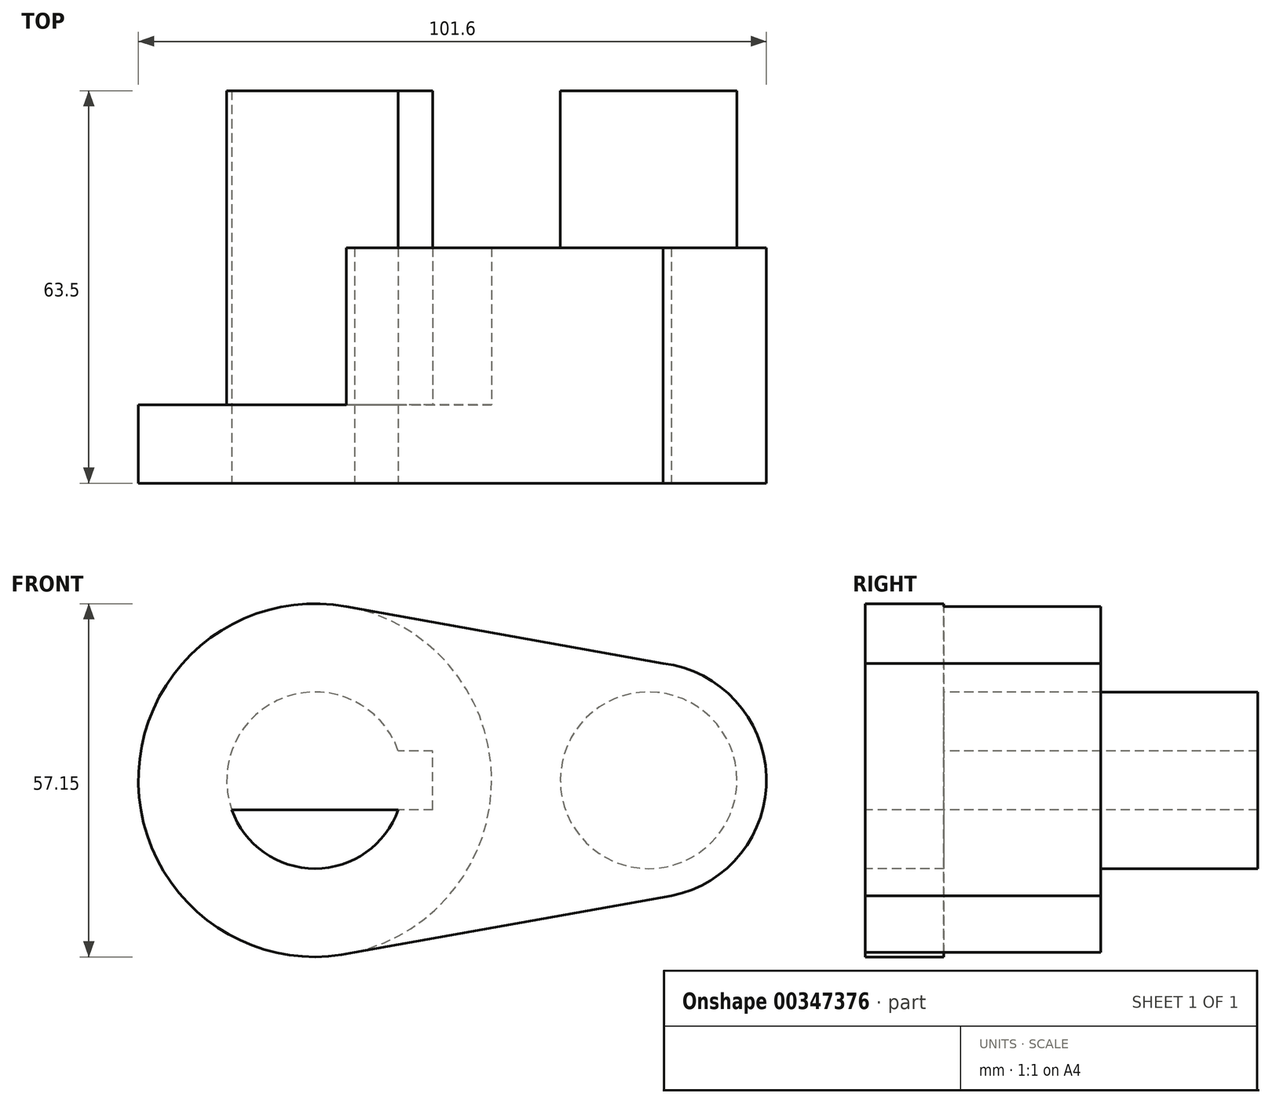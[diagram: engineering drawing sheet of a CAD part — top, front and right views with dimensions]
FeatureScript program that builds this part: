
annotation { "Feature Type Name" : "Feature", "Feature Type Description" : "" }
export const myFeature = defineFeature(function(context is Context, id is Id, definition is map)
    precondition{}
    {
        {
            var Q0;
            Q0=qCreatedBy(makeId("Front.planeOp"),FACE);
            var sketch = newSketch(context, id + "F0", { "sketchPlane" : qUnion([Q0])});
            skCircle(sketch, "E0", {"center": v(-15.51, -0.02) * mm, "radius": 28.58 * mm});
            skCircle(sketch, "E1", {"center": v(38.46, -0.02) * mm, "radius": 19.05 * mm});
            skCircle(sketch, "E2", {"center": v(-15.51, -0.02) * mm, "radius": 14.29 * mm});
            skCircle(sketch, "E3", {"center": v(38.46, -0.02) * mm, "radius": 14.29 * mm});
            skLineSegment(sketch, "E4.bottom", {"start": v(3.54, -4.79) * mm, "end": v(-34.56, -4.79) * mm});
            skLineSegment(sketch, "E4.top", {"start": v(3.54, 4.74) * mm, "end": v(-34.56, 4.74) * mm});
            skLineSegment(sketch, "E4.left", {"start": v(3.54, -4.79) * mm, "end": v(3.54, 4.74) * mm});
            skLineSegment(sketch, "E4.right", {"start": v(-34.56, -4.79) * mm, "end": v(-34.56, 4.74) * mm});
            skLineSegment(sketch, "E5", {"start": v(-10.46, 28.1) * mm, "end": v(40.77, 18.89) * mm});
            skLineSegment(sketch, "E6", {"start": v(-9.1, -27.87) * mm, "end": v(42.14, -18.71) * mm});
            skSolve(sketch);
        }
        {
            var Q0;
            {var subQ0=sQuery(id+"F0.wireOp",EDGE,"E4.top");var subQ1=sQuery(id+"F0.wireOp",EDGE,"E2");var subQ2=makeQuery(id+"F0.imprint","INTERSECT",VERTEX,{"disambiguationData":[OD(0.0)],"derivedFrom":[subQ1,subQ0]});Q0=makeQuery(id+"F0.imprint","IMPRINT",FACE,{"disambiguationData":[TD([[makeQuery(id+"F0.imprint","IMPRINT",EDGE,{"disambiguationData":[TD([[subQ2,-1.0]])],"derivedFrom":subQ1}),1.0]])]});}
            var Q1;
            {var subQ0=sQuery(id+"F0.wireOp",EDGE,"E4.top");var subQ1=sQuery(id+"F0.wireOp",EDGE,"E2");var subQ2=makeQuery(id+"F0.imprint","INTERSECT",VERTEX,{"disambiguationData":[OD(0.0)],"derivedFrom":[subQ1,subQ0]});Q1=makeQuery(id+"F0.imprint","IMPRINT",FACE,{"disambiguationData":[TD([[makeQuery(id+"F0.imprint","IMPRINT",EDGE,{"disambiguationData":[TD([[subQ2,1.0]])],"derivedFrom":subQ1}),1.0]])]});}
            var Q2;
            {var subQ0=sQuery(id+"F0.wireOp",EDGE,"E4.bottom");var subQ1=sQuery(id+"F0.wireOp",EDGE,"E2");var subQ2=makeQuery(id+"F0.imprint","INTERSECT",VERTEX,{"disambiguationData":[OD(0.0)],"derivedFrom":[subQ1,subQ0]});Q2=makeQuery(id+"F0.imprint","IMPRINT",FACE,{"disambiguationData":[TD([[makeQuery(id+"F0.imprint","IMPRINT",EDGE,{"disambiguationData":[TD([[subQ2,-1.0]])],"derivedFrom":subQ1}),1.0]])]});}
            var Q3;
            {var subQ5=sQuery(id+"F0.wireOp",EDGE,"E4.left");Q3=makeQuery(id+"F0.imprint","IMPRINT",FACE,{"disambiguationData":[TD([[makeQuery(id+"F0.imprint","IMPRINT",EDGE,{"derivedFrom":subQ5}),1.0]])]});}
            extrude(context, id + "F1", {"entities" : qUnion([Q0, Q1, Q2, Q3]), "oppositeDirection" : true, "depth" : 63.5 * mm});
        }
        {
            var Q0;
            {var subQ11=sQuery(id+"F0.wireOp",EDGE,"E4.left");Q0=makeQuery(id+"F0.imprint","IMPRINT",FACE,{"disambiguationData":[TD([[makeQuery(id+"F0.imprint","IMPRINT",EDGE,{"derivedFrom":subQ11}),-1.0]])]});}
            var Q1;
            {var subQ5=sQuery(id+"F0.wireOp",EDGE,"E4.right");Q1=makeQuery(id+"F0.imprint","IMPRINT",FACE,{"disambiguationData":[TD([[makeQuery(id+"F0.imprint","IMPRINT",EDGE,{"derivedFrom":subQ5}),-1.0]])]});}
            extrude(context, id + "F2", {"entities" : qUnion([Q0, Q1]), "operationType" : NewBodyOperationType.ADD, "oppositeDirection" : true, "depth" : 12.7 * mm});
        }
        {
            var Q0;
            {var subQ0=sQuery(id+"F0.wireOp",EDGE,"E5");Q0=makeQuery(id+"F0.imprint","IMPRINT",FACE,{"disambiguationData":[TD([[makeQuery(id+"F0.imprint","IMPRINT",EDGE,{"derivedFrom":subQ0}),-1.0]])]});}
            var Q1;
            Q1=makeQuery(id+"F0.imprint","IMPRINT",FACE,{"disambiguationData":[TD([[makeQuery(id+"F0.imprint","IMPRINT",EDGE,{"derivedFrom":sQuery(id+"F0.wireOp",EDGE,"E3")}),-1.0]])]});
            extrude(context, id + "F3", {"entities" : qUnion([Q0, Q1]), "operationType" : NewBodyOperationType.ADD, "oppositeDirection" : true, "depth" : 38.1 * mm});
        }
        {
            var Q0;
            Q0=makeQuery(id+"F0.imprint","IMPRINT",FACE,{"disambiguationData":[TD([[makeQuery(id+"F0.imprint","IMPRINT",EDGE,{"derivedFrom":sQuery(id+"F0.wireOp",EDGE,"E3")}),1.0]])]});
            extrude(context, id + "F4", {"entities" : qUnion([Q0]), "operationType" : NewBodyOperationType.ADD, "oppositeDirection" : true, "depth" : 63.5 * mm});
        }
    });
